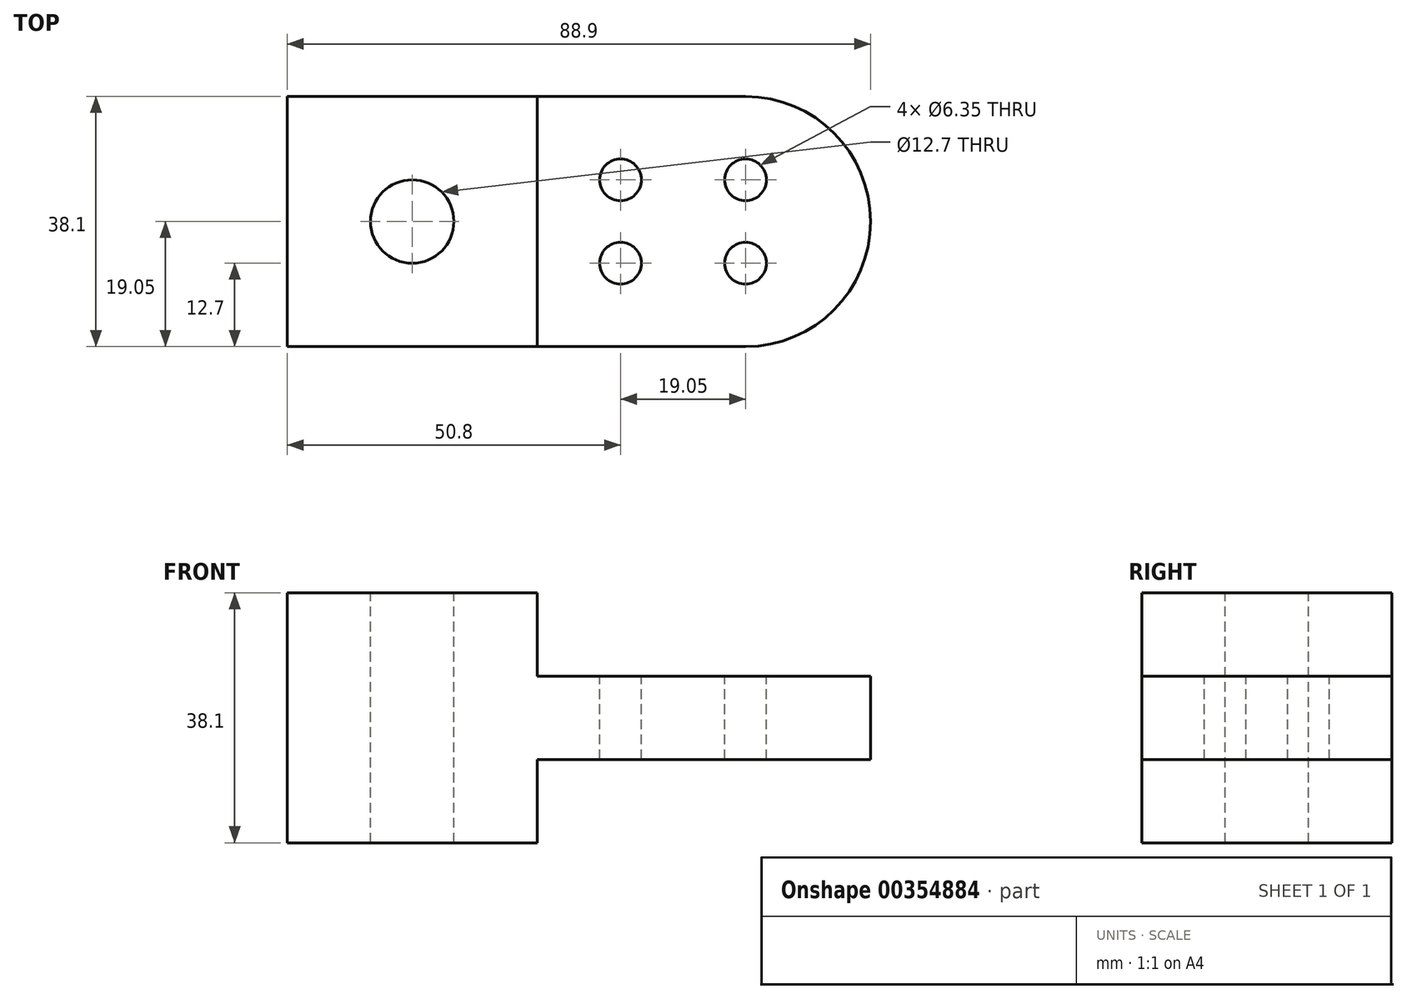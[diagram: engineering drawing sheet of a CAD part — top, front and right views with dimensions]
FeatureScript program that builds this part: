
annotation { "Feature Type Name" : "Feature", "Feature Type Description" : "" }
export const myFeature = defineFeature(function(context is Context, id is Id, definition is map)
    precondition{}
    {
        {
            var Q0;
            Q0=qCreatedBy(makeId("Front.planeOp"),FACE);
            var sketch = newSketch(context, id + "F0", { "sketchPlane" : qUnion([Q0])});
            skLineSegment(sketch, "E0.bottom", {"start": v(0, 0) * mm, "end": v(38.1, 0) * mm});
            skLineSegment(sketch, "E0.top", {"start": v(0, 38.1) * mm, "end": v(38.1, 38.1) * mm});
            skLineSegment(sketch, "E0.left", {"start": v(0, 0) * mm, "end": v(0, 38.1) * mm});
            skLineSegment(sketch, "E0.right", {"start": v(38.1, 0) * mm, "end": v(38.1, 38.1) * mm});
            skSolve(sketch);
        }
        {
            var Q0;
            Q0 = qSketchRegion(id + "F0", true);
            extrude(context, id + "F1", {"entities" : qUnion([Q0]), "depth" : 38.1 * mm});
        }
        {
            var Q0;
            Q0=makeQuery(id+"F1.opExtrude","SWEPT_FACE",FACE,{"disambiguationData":[OSD([sQuery(id+"F0.wireOp",EDGE,"E0.top")])]});
            var sketch = newSketch(context, id + "F2", { "sketchPlane" : qUnion([Q0])});
            skCircle(sketch, "E1", {"center": v(19.05, -19.05) * mm, "radius": 6.35 * mm});
            skPoint(sketch, "E1.centerSnap0", {"position": v(0, -19.05) * mm});
            skPoint(sketch, "E1.centerSnap1", {"position": v(19.05, 0) * mm});
            skSolve(sketch);
        }
        {
            var Q0;
            Q0 = qSketchRegion(id + "F2", true);
            extrude(context, id + "F3", {"entities" : qUnion([Q0]), "operationType" : NewBodyOperationType.REMOVE, "endBound" : BoundingType.THROUGH_ALL, "oppositeDirection" : true, "depth" : 25.4 * mm});
        }
        {
            var Q0;
            Q0=makeQuery(id+"F1.opExtrude","CAP_FACE",FACE,{"disambiguationData":[OSD([sQuery(id+"F0.wireOp",EDGE,"E0.bottom"),sQuery(id+"F0.wireOp",EDGE,"E0.top"),sQuery(id+"F0.wireOp",EDGE,"E0.left"),sQuery(id+"F0.wireOp",EDGE,"E0.right")])],"isStart":false});
            var sketch = newSketch(context, id + "F4", { "sketchPlane" : qUnion([Q0])});
            skLineSegment(sketch, "E2.bottom", {"start": v(38.1, 25.4) * mm, "end": v(69.85, 25.4) * mm});
            skLineSegment(sketch, "E2.top", {"start": v(38.1, 12.7) * mm, "end": v(69.85, 12.7) * mm});
            skLineSegment(sketch, "E2.left", {"start": v(38.1, 25.4) * mm, "end": v(38.1, 12.7) * mm});
            skLineSegment(sketch, "E2.right", {"start": v(69.85, 25.4) * mm, "end": v(69.85, 12.7) * mm});
            skSolve(sketch);
        }
        {
            var Q0;
            Q0 = qSketchRegion(id + "F4", true);
            extrude(context, id + "F5", {"entities" : qUnion([Q0]), "operationType" : NewBodyOperationType.ADD, "oppositeDirection" : true, "depth" : 38.1 * mm});
        }
        {
            var Q0;
            Q0=makeQuery(id+"F5.opExtrude","SWEPT_FACE",FACE,{"disambiguationData":[OSD([sQuery(id+"F4.wireOp",EDGE,"E2.bottom")])]});
            var sketch = newSketch(context, id + "F6", { "sketchPlane" : qUnion([Q0])});
            skArc(sketch, "E3", {"start": v(69.85, -38.1) * mm, "mid": v(88.9, -19.05) * mm, "end": v(69.85, 0) * mm});
            skLineSegment(sketch, "E4", {"start": v(69.85, 0) * mm, "end": v(69.85, -38.1) * mm});
            skSolve(sketch);
        }
        {
            var Q0;
            Q0 = qSketchRegion(id + "F6", true);
            extrude(context, id + "F7", {"entities" : qUnion([Q0]), "operationType" : NewBodyOperationType.ADD, "oppositeDirection" : true, "depth" : 12.7 * mm});
        }
        {
            var Q0;
            Q0=makeQuery(id+"F7.boolean.opBoolean","MERGE",FACE,{"derivedFrom":[makeQuery(id+"F5.opExtrude","SWEPT_FACE",FACE,{"disambiguationData":[OSD([sQuery(id+"F4.wireOp",EDGE,"E2.bottom")])]}),makeQuery(id+"F7.opExtrude","CAP_FACE",FACE,{"disambiguationData":[OSD([sQuery(id+"F6.wireOp",EDGE,"E3"),sQuery(id+"F6.wireOp",EDGE,"E4")])],"isStart":true})]});
            var sketch = newSketch(context, id + "F8", { "sketchPlane" : qUnion([Q0])});
            skCircle(sketch, "E5", {"center": v(50.8, -12.7) * mm, "radius": 3.18 * mm});
            skCircle(sketch, "E6", {"center": v(69.85, -12.7) * mm, "radius": 3.18 * mm});
            skCircle(sketch, "E7", {"center": v(50.8, -25.4) * mm, "radius": 3.18 * mm});
            skCircle(sketch, "E8", {"center": v(69.85, -25.4) * mm, "radius": 3.18 * mm});
            skSolve(sketch);
        }
        {
            var Q0;
            Q0 = qSketchRegion(id + "F8", true);
            extrude(context, id + "F9", {"entities" : qUnion([Q0]), "operationType" : NewBodyOperationType.REMOVE, "endBound" : BoundingType.THROUGH_ALL, "oppositeDirection" : true, "depth" : 25.4 * mm});
        }
    });
